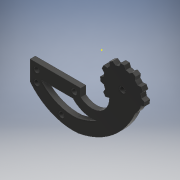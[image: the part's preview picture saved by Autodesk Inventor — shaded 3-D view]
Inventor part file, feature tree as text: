
AUTODESK INVENTOR PART (.ipt)
format: ipt  version: 2017 (Build 210142000, 142)  size: 268,288 bytes
history: native  units: mm
features: sketch x3, extrude x2, hole x2
ambient origin geometry x8: Origin, YZ Plane, XZ Plane, XY Plane, X Axis, Y Axis, Z Axis, Center Point
bodies: Body1 (feature_tree)
feature tree (7):
  extrude  "Extrusion2"  Depth=30.0mm
  sketch  "Esquisse2"
  extrude  "Extrusion3"  TaperAngle=90.0deg  [1 undecoded]
  hole  "Perçage1"  [1 undecoded]
  hole  "Perçage2"  [1 undecoded]
  sketch  "Esquisse1"
  sketch  "Esquisse6"
note: 3 required parameter values undecoded (feature->parameter linkage not recoverable at this tier; creation-order binding heuristic only, values carry confidence <= 0.55)
